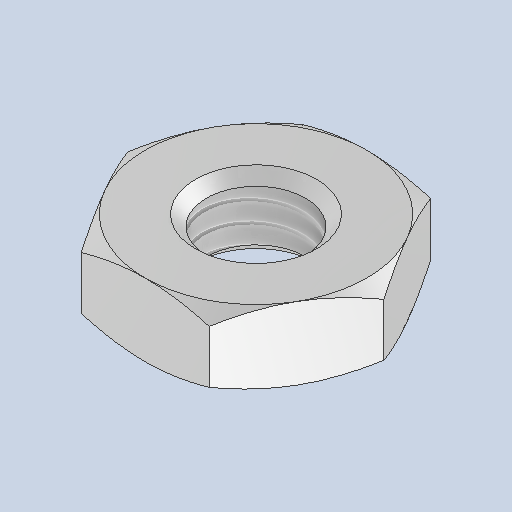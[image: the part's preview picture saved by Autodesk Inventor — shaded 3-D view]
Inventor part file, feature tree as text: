
AUTODESK INVENTOR PART (.ipt)
format: ipt  version: 2024.2 (Build 282272000, 272)  size: 166,912 bytes
history: native  units: mm
features: sketch x2, revolve x1, extrude x1, hole x1, mirror x1
ambient origin geometry x8: Origin, YZ Plane, XZ Plane, XY Plane, X Axis, Y Axis, Z Axis, Center Point
bodies: Solid1 (feature_tree)
feature tree (6):
  revolve  "Revolution1"  [1 undecoded]
  sketch  "Sketch2"  dims[d2=6.350853mm d3=30.0deg d4=90.0deg d5=0.0mm d6=0.0mm d7=2.459mm d8=6.0mm d9=3.0mm d10=2.0mm d11=90.0deg d12=6.0mm d13=0.0mm]
  extrude  "Extrusion1"  TaperAngle=30.0deg  [1 undecoded]
  hole  "Hole1"  [1 undecoded]
  mirror  "Mirror1"
  sketch  "Sketch1"  dims[d0=1.8mm d1=5.5mm]
note: 3 required parameter values undecoded (feature->parameter linkage not recoverable at this tier; creation-order binding heuristic only, values carry confidence <= 0.55)